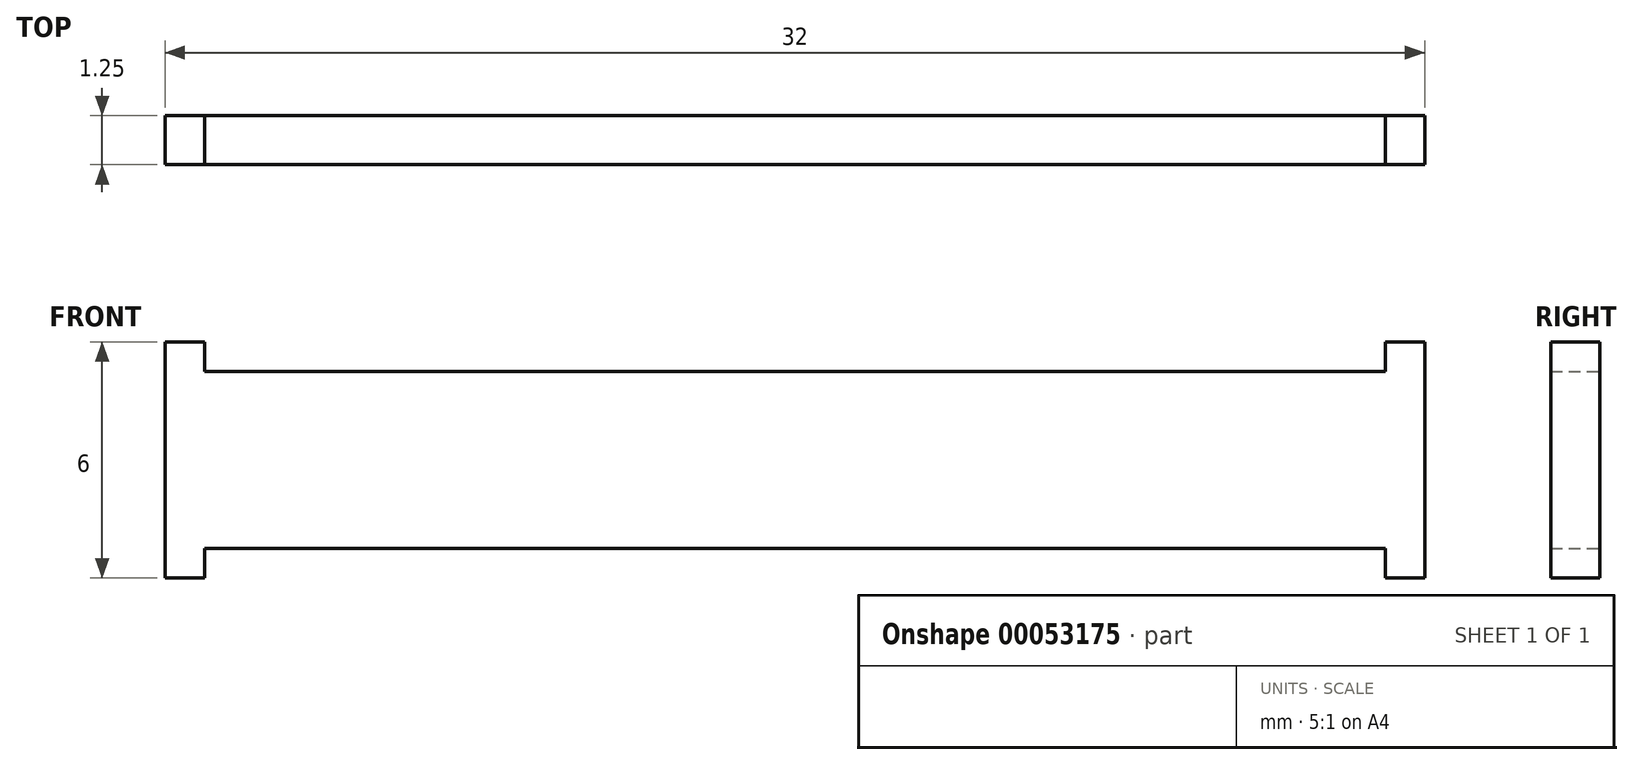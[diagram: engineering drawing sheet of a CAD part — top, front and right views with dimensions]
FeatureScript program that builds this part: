
annotation { "Feature Type Name" : "Feature", "Feature Type Description" : "" }
export const myFeature = defineFeature(function(context is Context, id is Id, definition is map)
    precondition{}
    {
        {
            var Q0;
            Q0=qCreatedBy(makeId("Front.planeOp"),FACE);
            var sketch = newSketch(context, id + "F0", { "sketchPlane" : qUnion([Q0])});
            skLineSegment(sketch, "E0.bottom", {"start": v(0, 0) * mm, "end": v(30, 0) * mm});
            skLineSegment(sketch, "E0.top", {"start": v(0, 4.5) * mm, "end": v(30, 4.5) * mm});
            skLineSegment(sketch, "E0.left", {"start": v(0, 0) * mm, "end": v(0, 4.5) * mm});
            skLineSegment(sketch, "E0.right", {"start": v(30, 0) * mm, "end": v(30, 4.5) * mm});
            skSolve(sketch);
        }
        {
            var Q0;
            Q0=makeQuery(id+"F0.imprint","IMPRINT",FACE,{"disambiguationData":[TD([[makeQuery(id+"F0.imprint","IMPRINT",EDGE,{"derivedFrom":sQuery(id+"F0.wireOp",EDGE,"E0.bottom")}),1.0]])]});
            extrude(context, id + "F1", {"entities" : qUnion([Q0]), "depth" : 1.25 * mm});
        }
        {
            var Q0;
            Q0=makeQuery(id+"F1.opExtrude","CAP_FACE",FACE,{"disambiguationData":[OSD([sQuery(id+"F0.wireOp",EDGE,"E0.bottom"),sQuery(id+"F0.wireOp",EDGE,"E0.top"),sQuery(id+"F0.wireOp",EDGE,"E0.left"),sQuery(id+"F0.wireOp",EDGE,"E0.right")])],"isStart":false});
            var sketch = newSketch(context, id + "F2", { "sketchPlane" : qUnion([Q0])});
            skLineSegment(sketch, "E1", {"start": v(0, 4.5) * mm, "end": v(0, 5.25) * mm});
            skLineSegment(sketch, "E2", {"start": v(0, 5.25) * mm, "end": v(-1, 5.25) * mm});
            skLineSegment(sketch, "E3", {"start": v(-1, 5.25) * mm, "end": v(-1, -0.75) * mm});
            skLineSegment(sketch, "E4", {"start": v(-1, -0.75) * mm, "end": v(0, -0.75) * mm});
            skLineSegment(sketch, "E5", {"start": v(0, -0.75) * mm, "end": v(0, 0) * mm});
            skLineSegment(sketch, "E6", {"start": v(30, 4.5) * mm, "end": v(30, 5.25) * mm});
            skPoint(sketch, "E6.endSnap0", {"position": v(-0.5, 5.25) * mm});
            skLineSegment(sketch, "E7", {"start": v(30, 5.25) * mm, "end": v(31, 5.25) * mm});
            skLineSegment(sketch, "E8", {"start": v(31, 5.25) * mm, "end": v(31, -0.75) * mm});
            skLineSegment(sketch, "E9", {"start": v(31, -0.75) * mm, "end": v(30, -0.75) * mm});
            skLineSegment(sketch, "E10", {"start": v(30, -0.75) * mm, "end": v(30, 0) * mm});
            skLineSegment(sketch, "E11", {"start": v(0, 4.5) * mm, "end": v(0, 0) * mm});
            skLineSegment(sketch, "E12", {"start": v(30, 4.5) * mm, "end": v(30, 0) * mm});
            skSolve(sketch);
        }
        {
            var Q0;
            Q0 = qSketchRegion(id + "F2", true);
            extrude(context, id + "F3", {"entities" : qUnion([Q0]), "operationType" : NewBodyOperationType.ADD, "oppositeDirection" : true, "depth" : 1.25 * mm});
        }
    });
